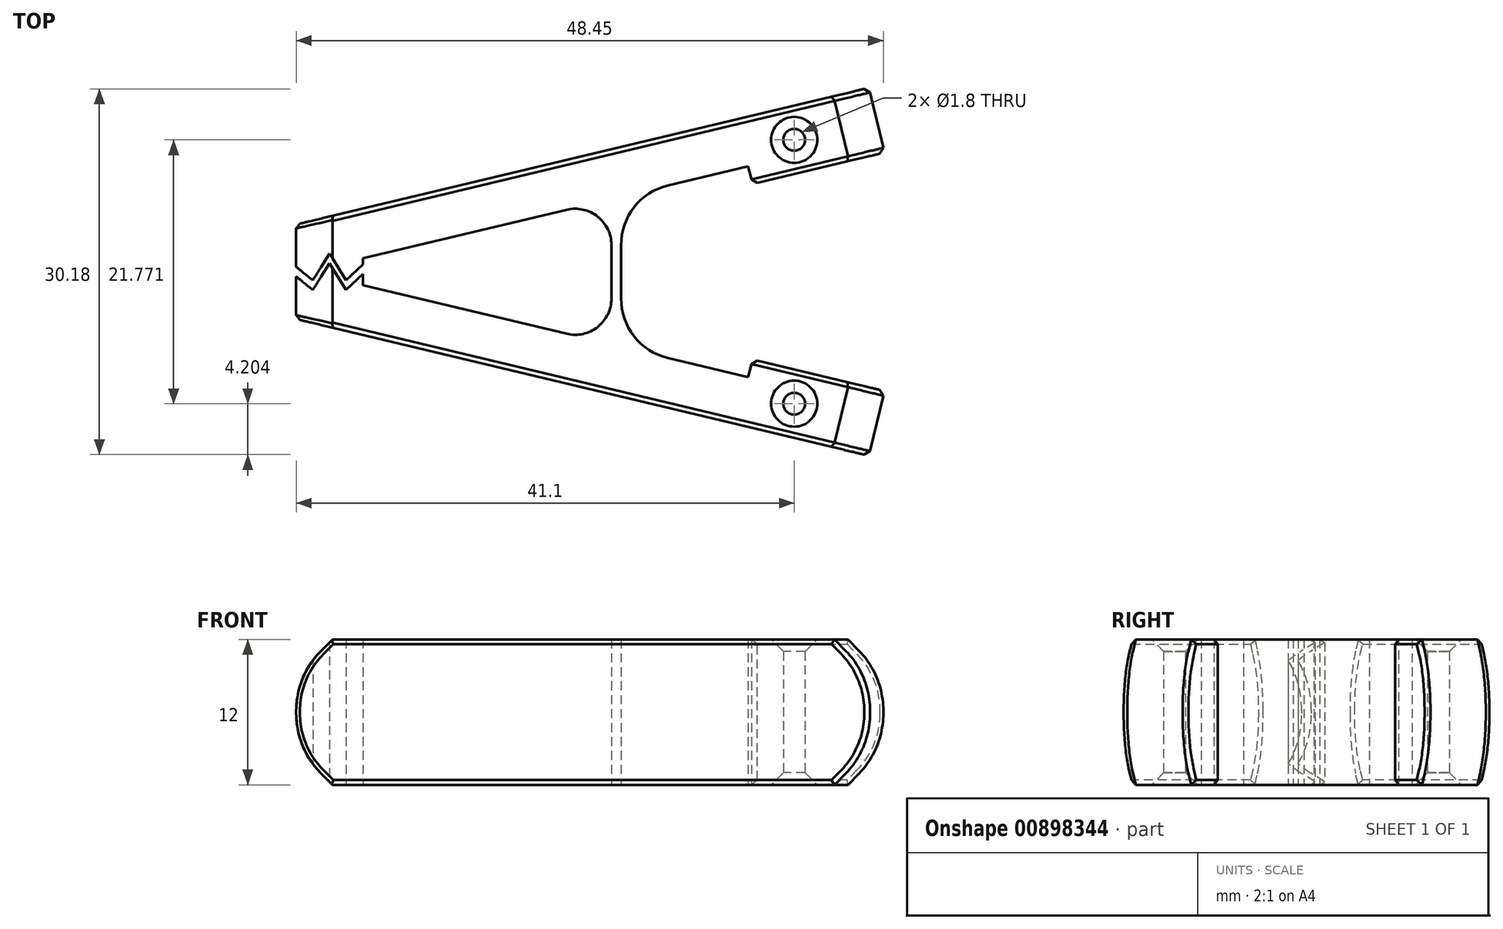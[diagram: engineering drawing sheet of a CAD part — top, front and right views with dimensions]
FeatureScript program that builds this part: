
annotation { "Feature Type Name" : "Feature", "Feature Type Description" : "" }
export const myFeature = defineFeature(function(context is Context, id is Id, definition is map)
    precondition{}
    {
        {
            var Q0;
            Q0=qCreatedBy(makeId("Top.planeOp"),FACE);
            var sketch = newSketch(context, id + "F0", { "sketchPlane" : qUnion([Q0])});
            skLineSegment(sketch, "E0", {"start": v(0, 0) * mm, "end": v(0, 4.65) * mm});
            skLineSegment(sketch, "E1", {"start": v(10.83, 7.24) * mm, "end": v(21.73, 9.84) * mm});
            skLineSegment(sketch, "E2", {"start": v(21.73, 9.84) * mm, "end": v(20.45, 15.19) * mm});
            skLineSegment(sketch, "E3", {"start": v(20.45, 15.19) * mm, "end": v(-26.82, 3.9) * mm});
            skLineSegment(sketch, "E4", {"start": v(-26.82, 3.9) * mm, "end": v(-26.82, 0.4) * mm});
            skLineSegment(sketch, "E5", {"start": v(-21.32, 0.6) * mm, "end": v(-21.32, 1.1) * mm});
            skLineSegment(sketch, "E6", {"start": v(-21.32, 1.1) * mm, "end": v(-4.5, 5.12) * mm});
            skLineSegment(sketch, "E7", {"start": v(-0.8, 2.2) * mm, "end": v(-0.8, 0) * mm});
            skLineSegment(sketch, "E8", {"start": v(3.84, 7.1) * mm, "end": v(10.48, 8.7) * mm});
            skLineSegment(sketch, "E9", {"start": v(10.48, 8.7) * mm, "end": v(10.83, 7.24) * mm});
            skPoint(sketch, "E10.visualSharp", {"position": v(-0.8, 6) * mm});
            skArc(sketch, "E10.filletArc", {"start": v(-0.8, 2.2) * mm, "mid": v(-1.94, 4.55) * mm, "end": v(-4.5, 5.12) * mm});
            skPoint(sketch, "E11.visualSharp", {"position": v(-0.02, 6.19) * mm});
            skArc(sketch, "E11.filletArc", {"start": v(3.84, 7.1) * mm, "mid": v(1.06, 5.32) * mm, "end": v(0, 2.2) * mm});
            skLineSegment(sketch, "E12.MirrorCS", {"start": v(-26.82, -3.9) * mm, "end": v(-26.82, -0.4) * mm});
            skLineSegment(sketch, "E13.MirrorCS", {"start": v(20.45, -15.19) * mm, "end": v(-26.82, -3.9) * mm});
            skLineSegment(sketch, "E14.MirrorCS", {"start": v(21.73, -9.84) * mm, "end": v(20.45, -15.19) * mm});
            skLineSegment(sketch, "E15.MirrorCS", {"start": v(10.83, -7.24) * mm, "end": v(21.73, -9.84) * mm});
            skLineSegment(sketch, "E16.MirrorCS", {"start": v(10.48, -8.7) * mm, "end": v(10.83, -7.24) * mm});
            skLineSegment(sketch, "E17.MirrorCS", {"start": v(3.84, -7.1) * mm, "end": v(10.48, -8.7) * mm});
            skArc(sketch, "E18.MirrorCS", {"start": v(3.84, -7.1) * mm, "mid": v(1.06, -5.32) * mm, "end": v(0, -2.2) * mm});
            skLineSegment(sketch, "E19.MirrorCS", {"start": v(0, 0) * mm, "end": v(0, -2.2) * mm});
            skLineSegment(sketch, "E20.MirrorCS", {"start": v(-0.8, -2.2) * mm, "end": v(-0.8, 0) * mm});
            skArc(sketch, "E21.MirrorCS", {"start": v(-0.8, -2.2) * mm, "mid": v(-1.94, -4.55) * mm, "end": v(-4.5, -5.12) * mm});
            skLineSegment(sketch, "E22.MirrorCS", {"start": v(-21.32, -1.1) * mm, "end": v(-4.5, -5.12) * mm});
            skLineSegment(sketch, "E23.MirrorCS", {"start": v(-21.32, -0.2) * mm, "end": v(-21.32, -1.1) * mm});
            skPoint(sketch, "E24.orphan", {"position": v(0, -4.65) * mm});
            skLineSegment(sketch, "E25", {"start": v(-21.32, 0.2) * mm, "end": v(-22.7, -1.1) * mm, "construction": true});
            skLineSegment(sketch, "E26", {"start": v(-22.7, -1.1) * mm, "end": v(-24.07, 1.1) * mm, "construction": true});
            skLineSegment(sketch, "E27", {"start": v(-24.07, 1.1) * mm, "end": v(-25.45, -1.1) * mm, "construction": true});
            skLineSegment(sketch, "E28", {"start": v(-25.45, -1.1) * mm, "end": v(-26.82, 0) * mm, "construction": true});
            skLineSegment(sketch, "E29", {"start": v(-21.32, 1.1) * mm, "end": v(-24.07, 1.1) * mm, "construction": true});
            skLineSegment(sketch, "E30", {"start": v(-21.32, -1.1) * mm, "end": v(-22.7, -1.1) * mm, "construction": true});
            skLineSegment(sketch, "E31", {"start": v(-25.45, -1.1) * mm, "end": v(-22.7, -1.1) * mm, "construction": true});
            skLineSegment(sketch, "E32", {"start": v(-26.82, -0.4) * mm, "end": v(-25.45, -1.5) * mm});
            skLineSegment(sketch, "E33", {"start": v(-25.45, -1.5) * mm, "end": v(-24.07, 0.7) * mm});
            skLineSegment(sketch, "E34", {"start": v(-24.07, 0.7) * mm, "end": v(-22.7, -1.5) * mm});
            skLineSegment(sketch, "E35", {"start": v(-22.7, -1.5) * mm, "end": v(-21.32, -0.2) * mm});
            skLineSegment(sketch, "E36", {"start": v(-26.82, 0.4) * mm, "end": v(-25.45, -0.7) * mm});
            skLineSegment(sketch, "E37", {"start": v(-25.45, -0.7) * mm, "end": v(-24.07, 1.5) * mm});
            skLineSegment(sketch, "E38", {"start": v(-24.07, 1.5) * mm, "end": v(-22.7, -0.7) * mm});
            skLineSegment(sketch, "E39", {"start": v(-22.7, -0.7) * mm, "end": v(-21.32, 0.6) * mm});
            skPoint(sketch, "E40.orphan", {"position": v(-26.82, 0) * mm});
            skCircle(sketch, "E41", {"center": v(14.28, 10.89) * mm, "radius": 0.9 * mm});
            skCircle(sketch, "E42.MirrorC", {"center": v(14.28, -10.89) * mm, "radius": 0.9 * mm});
            skSolve(sketch);
        }
        {
            var Q0;
            Q0=makeQuery(id+"F0.imprint","IMPRINT",FACE,{"disambiguationData":[TD([[makeQuery(id+"F0.imprint","IMPRINT",EDGE,{"derivedFrom":sQuery(id+"F0.wireOp",EDGE,"E1")}),1.0]])]});
            extrude(context, id + "F1", {"entities" : qUnion([Q0]), "depth" : 12 * mm, "offsetDistance" : 25 * mm});
        }
        {
            var Q0;
            Q0=makeQuery(id+"F1.opExtrude","CAP_EDGE",EDGE,{"disambiguationData":[OSD([sQuery(id+"F0.wireOp",EDGE,"E12.MirrorCS")])],"isStart":true});
            var Q1;
            Q1=makeQuery(id+"F1.opExtrude","CAP_EDGE",EDGE,{"disambiguationData":[OSD([sQuery(id+"F0.wireOp",EDGE,"E4")])],"isStart":true});
            var Q2;
            Q2=makeQuery(id+"F1.opExtrude","CAP_EDGE",EDGE,{"disambiguationData":[OSD([sQuery(id+"F0.wireOp",EDGE,"E12.MirrorCS")])],"isStart":false});
            var Q3;
            Q3=makeQuery(id+"F1.opExtrude","CAP_EDGE",EDGE,{"disambiguationData":[OSD([sQuery(id+"F0.wireOp",EDGE,"E4")])],"isStart":false});
            var Q4;
            Q4=makeQuery(id+"F1.opExtrude","CAP_EDGE",EDGE,{"disambiguationData":[OSD([sQuery(id+"F0.wireOp",EDGE,"E14.MirrorCS")])],"isStart":true});
            var Q5;
            Q5=makeQuery(id+"F1.opExtrude","CAP_EDGE",EDGE,{"disambiguationData":[OSD([sQuery(id+"F0.wireOp",EDGE,"E2")])],"isStart":true});
            var Q6;
            Q6=makeQuery(id+"F1.opExtrude","CAP_EDGE",EDGE,{"disambiguationData":[OSD([sQuery(id+"F0.wireOp",EDGE,"E14.MirrorCS")])],"isStart":false});
            var Q7;
            Q7=makeQuery(id+"F1.opExtrude","CAP_EDGE",EDGE,{"disambiguationData":[OSD([sQuery(id+"F0.wireOp",EDGE,"E2")])],"isStart":false});
            chamfer(context, id + "F2", {"entities" : qUnion([Q0, Q1, Q2, Q3, Q4, Q5, Q6, Q7]), "width" : (12 / 4) * mm, "tangentPropagation" : true});
        }
        {
            var Q0;
            Q0=makeQuery(id+"F1.opExtrude","CAP_EDGE",EDGE,{"disambiguationData":[OSD([sQuery(id+"F0.wireOp",EDGE,"E42.MirrorC")])],"isStart":true});
            var Q1;
            Q1=makeQuery(id+"F1.opExtrude","CAP_EDGE",EDGE,{"disambiguationData":[OSD([sQuery(id+"F0.wireOp",EDGE,"E41")])],"isStart":true});
            var Q2;
            Q2=makeQuery(id+"F1.opExtrude","CAP_EDGE",EDGE,{"disambiguationData":[OSD([sQuery(id+"F0.wireOp",EDGE,"E41")])],"isStart":false});
            var Q3;
            Q3=makeQuery(id+"F1.opExtrude","CAP_EDGE",EDGE,{"disambiguationData":[OSD([sQuery(id+"F0.wireOp",EDGE,"E42.MirrorC")])],"isStart":false});
            chamfer(context, id + "F3", {"entities" : qUnion([Q0, Q1, Q2, Q3]), "width" : 1 * mm, "tangentPropagation" : true});
        }
        {
            var Q0;
            {var subQ0=sQuery(id+"F0.wireOp",EDGE,"E4");Q0=makeQuery(id+"F2.opChamfer","BLEND_EDGE",EDGE,{"blendedFrom":[makeQuery(id+"F1.opExtrude","CAP_EDGE",EDGE,{"disambiguationData":[OSD([subQ0])],"isStart":false}),makeQuery(id+"F1.opExtrude","SWEPT_FACE",FACE,{"disambiguationData":[OSD([subQ0])]})],"blendedInto":[makeQuery(id+"F1.opExtrude","SWEPT_FACE",FACE,{"disambiguationData":[OSD([subQ0])]})]});}
            var Q1;
            {var subQ0=sQuery(id+"F0.wireOp",EDGE,"E12.MirrorCS");Q1=makeQuery(id+"F2.opChamfer","BLEND_EDGE",EDGE,{"blendedFrom":[makeQuery(id+"F1.opExtrude","CAP_EDGE",EDGE,{"disambiguationData":[OSD([subQ0])],"isStart":false}),makeQuery(id+"F1.opExtrude","SWEPT_FACE",FACE,{"disambiguationData":[OSD([subQ0])]})],"blendedInto":[makeQuery(id+"F1.opExtrude","SWEPT_FACE",FACE,{"disambiguationData":[OSD([subQ0])]})]});}
            var Q2;
            {var subQ0=sQuery(id+"F0.wireOp",EDGE,"E4");Q2=makeQuery(id+"F2.opChamfer","BLEND_EDGE",EDGE,{"blendedFrom":[makeQuery(id+"F1.opExtrude","CAP_EDGE",EDGE,{"disambiguationData":[OSD([subQ0])],"isStart":true}),makeQuery(id+"F1.opExtrude","SWEPT_FACE",FACE,{"disambiguationData":[OSD([subQ0])]})],"blendedInto":[makeQuery(id+"F1.opExtrude","SWEPT_FACE",FACE,{"disambiguationData":[OSD([subQ0])]})]});}
            var Q3;
            {var subQ0=sQuery(id+"F0.wireOp",EDGE,"E12.MirrorCS");Q3=makeQuery(id+"F2.opChamfer","BLEND_EDGE",EDGE,{"blendedFrom":[makeQuery(id+"F1.opExtrude","CAP_EDGE",EDGE,{"disambiguationData":[OSD([subQ0])],"isStart":true}),makeQuery(id+"F1.opExtrude","SWEPT_FACE",FACE,{"disambiguationData":[OSD([subQ0])]})],"blendedInto":[makeQuery(id+"F1.opExtrude","SWEPT_FACE",FACE,{"disambiguationData":[OSD([subQ0])]})]});}
            var Q4;
            {var subQ0=sQuery(id+"F0.wireOp",EDGE,"E2");Q4=makeQuery(id+"F2.opChamfer","BLEND_EDGE",EDGE,{"blendedFrom":[makeQuery(id+"F1.opExtrude","CAP_EDGE",EDGE,{"disambiguationData":[OSD([subQ0])],"isStart":false}),makeQuery(id+"F1.opExtrude","SWEPT_FACE",FACE,{"disambiguationData":[OSD([subQ0])]})],"blendedInto":[makeQuery(id+"F1.opExtrude","SWEPT_FACE",FACE,{"disambiguationData":[OSD([subQ0])]})]});}
            var Q5;
            {var subQ0=sQuery(id+"F0.wireOp",EDGE,"E2");Q5=makeQuery(id+"F2.opChamfer","BLEND_EDGE",EDGE,{"blendedFrom":[makeQuery(id+"F1.opExtrude","CAP_EDGE",EDGE,{"disambiguationData":[OSD([subQ0])],"isStart":true}),makeQuery(id+"F1.opExtrude","SWEPT_FACE",FACE,{"disambiguationData":[OSD([subQ0])]})],"blendedInto":[makeQuery(id+"F1.opExtrude","SWEPT_FACE",FACE,{"disambiguationData":[OSD([subQ0])]})]});}
            var Q6;
            {var subQ0=sQuery(id+"F0.wireOp",EDGE,"E14.MirrorCS");Q6=makeQuery(id+"F2.opChamfer","BLEND_EDGE",EDGE,{"blendedFrom":[makeQuery(id+"F1.opExtrude","CAP_EDGE",EDGE,{"disambiguationData":[OSD([subQ0])],"isStart":true}),makeQuery(id+"F1.opExtrude","SWEPT_FACE",FACE,{"disambiguationData":[OSD([subQ0])]})],"blendedInto":[makeQuery(id+"F1.opExtrude","SWEPT_FACE",FACE,{"disambiguationData":[OSD([subQ0])]})]});}
            var Q7;
            {var subQ0=sQuery(id+"F0.wireOp",EDGE,"E14.MirrorCS");Q7=makeQuery(id+"F2.opChamfer","BLEND_EDGE",EDGE,{"blendedFrom":[makeQuery(id+"F1.opExtrude","CAP_EDGE",EDGE,{"disambiguationData":[OSD([subQ0])],"isStart":false}),makeQuery(id+"F1.opExtrude","SWEPT_FACE",FACE,{"disambiguationData":[OSD([subQ0])]})],"blendedInto":[makeQuery(id+"F1.opExtrude","SWEPT_FACE",FACE,{"disambiguationData":[OSD([subQ0])]})]});}
            fillet(context, id + "F4", {"entities" : qUnion([Q0, Q1, Q2, Q3, Q4, Q5, Q6, Q7]), "tangentPropagation" : true, "radius" : 7 * mm, "defaultsChanged" : true, "vertexSettings" : [], "allowEdgeOverflow" : false});
        }
        {
            var Q0;
            Q0=makeQuery(id+"F1.opExtrude","SWEPT_FACE",FACE,{"disambiguationData":[OSD([sQuery(id+"F0.wireOp",EDGE,"E3")])]});
            var Q1;
            Q1=makeQuery(id+"F1.opExtrude","SWEPT_FACE",FACE,{"disambiguationData":[OSD([sQuery(id+"F0.wireOp",EDGE,"E13.MirrorCS")])]});
            var Q2;
            Q2=makeQuery(id+"F1.opExtrude","SWEPT_FACE",FACE,{"disambiguationData":[OSD([sQuery(id+"F0.wireOp",EDGE,"E1")])]});
            var Q3;
            Q3=makeQuery(id+"F1.opExtrude","SWEPT_FACE",FACE,{"disambiguationData":[OSD([sQuery(id+"F0.wireOp",EDGE,"E15.MirrorCS")])]});
            chamfer(context, id + "F5", {"entities" : qUnion([Q0, Q1, Q2, Q3]), "width" : 0.4 * mm, "tangentPropagation" : true});
        }
    });
